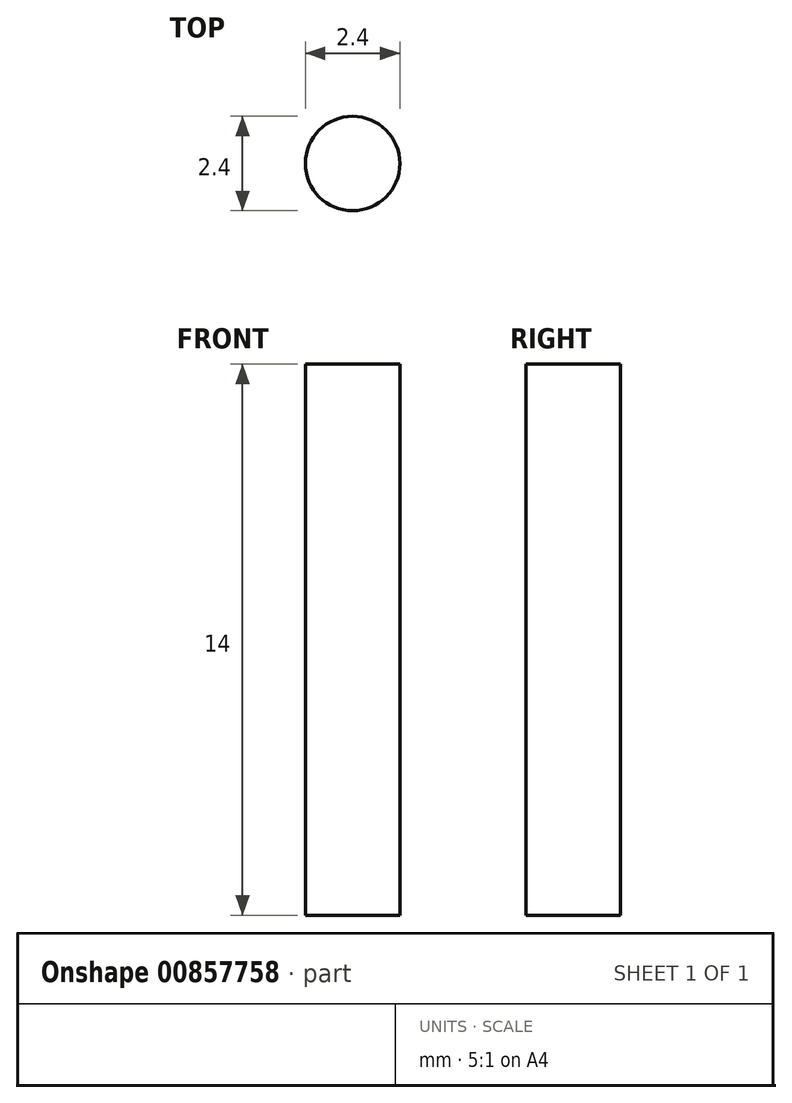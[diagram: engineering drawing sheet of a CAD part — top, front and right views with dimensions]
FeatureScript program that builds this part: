
annotation { "Feature Type Name" : "Feature", "Feature Type Description" : "" }
export const myFeature = defineFeature(function(context is Context, id is Id, definition is map)
    precondition{}
    {
        {
            var Q0;
            Q0=qCreatedBy(makeId("Top.planeOp"),FACE);
            var sketch = newSketch(context, id + "F0", { "sketchPlane" : qUnion([Q0])});
            skCircle(sketch, "E0", {"center": v(0, 0) * mm, "radius": 1.2 * mm});
            skSolve(sketch);
        }
        {
            var Q0;
            Q0=makeQuery(id+"F0.imprint","IMPRINT",FACE,{"disambiguationData":[TD([[makeQuery(id+"F0.imprint","IMPRINT",EDGE,{"derivedFrom":sQuery(id+"F0.wireOp",EDGE,"E0")}),1.0]])]});
            extrude(context, id + "F1", {"entities" : qUnion([Q0]), "depth" : 14 * mm, "offsetDistance" : 25 * mm});
        }
    });
